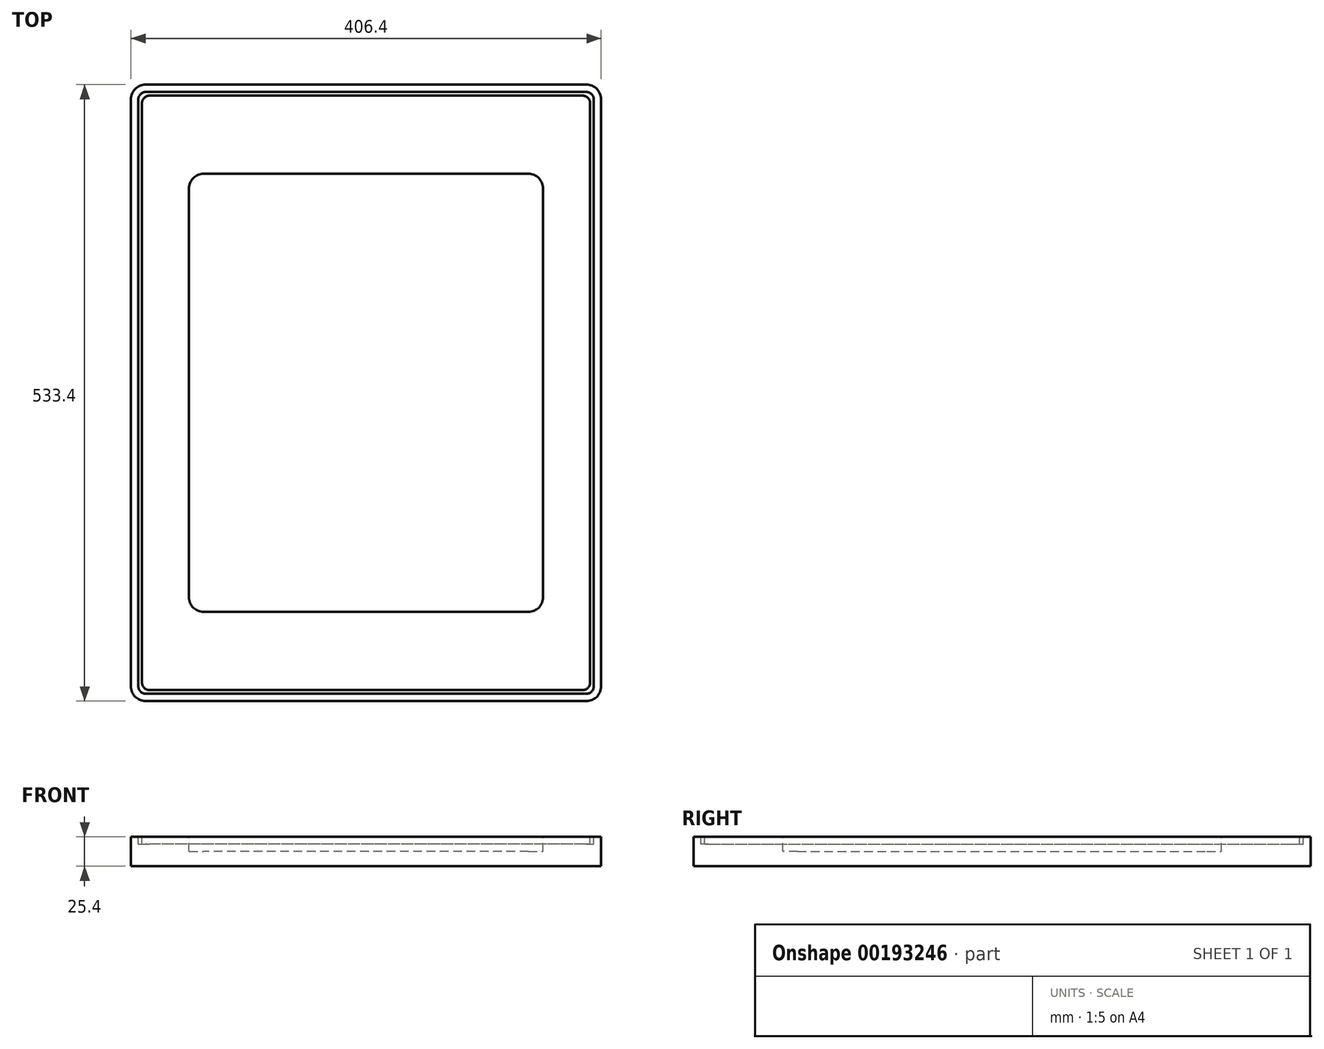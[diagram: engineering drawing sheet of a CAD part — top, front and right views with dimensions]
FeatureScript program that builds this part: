
annotation { "Feature Type Name" : "Feature", "Feature Type Description" : "" }
export const myFeature = defineFeature(function(context is Context, id is Id, definition is map)
    precondition{}
    {
        {
            var Q0;
            Q0=qCreatedBy(makeId("Top.planeOp"),FACE);
            var sketch = newSketch(context, id + "F0", { "sketchPlane" : qUnion([Q0])});
            skLineSegment(sketch, "E0.bottom", {"start": v(203.2, -266.7) * mm, "end": v(-203.2, -266.7) * mm});
            skLineSegment(sketch, "E0.top", {"start": v(203.2, 266.7) * mm, "end": v(-203.2, 266.7) * mm});
            skLineSegment(sketch, "E0.left", {"start": v(203.2, -266.7) * mm, "end": v(203.2, 266.7) * mm});
            skLineSegment(sketch, "E0.right", {"start": v(-203.2, -266.7) * mm, "end": v(-203.2, 266.7) * mm});
            skPoint(sketch, "E0.middle", {"position": v(0, 0) * mm});
            skSolve(sketch);
        }
        {
            var Q0;
            Q0=makeQuery(id+"F0.imprint","IMPRINT",FACE,{"disambiguationData":[TD([[makeQuery(id+"F0.imprint","IMPRINT",EDGE,{"derivedFrom":sQuery(id+"F0.wireOp",EDGE,"E0.bottom")}),-1.0]])]});
            extrude(context, id + "F1", {"entities" : qUnion([Q0]), "depth" : 25.4 * mm});
        }
        {
            var Q0;
            Q0=makeQuery(id+"F1.opExtrude","CAP_FACE",FACE,{"disambiguationData":[OSD([sQuery(id+"F0.wireOp",EDGE,"E0.bottom"),sQuery(id+"F0.wireOp",EDGE,"E0.top"),sQuery(id+"F0.wireOp",EDGE,"E0.left"),sQuery(id+"F0.wireOp",EDGE,"E0.right")])],"isStart":false});
            var sketch = newSketch(context, id + "F2", { "sketchPlane" : qUnion([Q0])});
            skLineSegment(sketch, "E1.bottom", {"start": v(153.03, -189.55) * mm, "end": v(-153.04, -189.55) * mm});
            skLineSegment(sketch, "E1.top", {"start": v(153.03, 189.55) * mm, "end": v(-153.04, 189.55) * mm});
            skLineSegment(sketch, "E1.left", {"start": v(153.03, -189.55) * mm, "end": v(153.03, 189.55) * mm});
            skLineSegment(sketch, "E1.right", {"start": v(-153.04, -189.55) * mm, "end": v(-153.04, 189.55) * mm});
            skPoint(sketch, "E1.middle", {"position": v(0, 0) * mm});
            skSolve(sketch);
        }
        {
            var Q0;
            Q0 = qSketchRegion(id + "F2", true);
            extrude(context, id + "F3", {"entities" : qUnion([Q0]), "operationType" : NewBodyOperationType.REMOVE, "oppositeDirection" : true, "depth" : 12.7 * mm});
        }
        {
            var Q0;
            Q0=makeQuery(id+"F1.opExtrude","SWEPT_EDGE",EDGE,{"disambiguationData":[OSD([sQuery(id+"F0.wireOp",EDGE,"E0.bottom"),sQuery(id+"F0.wireOp",EDGE,"E0.right")])]});
            var Q1;
            Q1=makeQuery(id+"F1.opExtrude","SWEPT_EDGE",EDGE,{"disambiguationData":[OSD([sQuery(id+"F0.wireOp",EDGE,"E0.bottom"),sQuery(id+"F0.wireOp",EDGE,"E0.left")])]});
            var Q2;
            Q2=makeQuery(id+"F1.opExtrude","SWEPT_EDGE",EDGE,{"disambiguationData":[OSD([sQuery(id+"F0.wireOp",EDGE,"E0.top"),sQuery(id+"F0.wireOp",EDGE,"E0.left")])]});
            var Q3;
            Q3=makeQuery(id+"F1.opExtrude","SWEPT_EDGE",EDGE,{"disambiguationData":[OSD([sQuery(id+"F0.wireOp",EDGE,"E0.top"),sQuery(id+"F0.wireOp",EDGE,"E0.right")])]});
            var Q4;
            Q4=makeQuery(id+"F3.boolean.opBoolean","COPY",EDGE,{"derivedFrom":makeQuery(id+"F3.opExtrude","SWEPT_EDGE",EDGE,{"disambiguationData":[OSD([sQuery(id+"F2.wireOp",EDGE,"E1.top"),sQuery(id+"F2.wireOp",EDGE,"E1.right")])]})});
            var Q5;
            Q5=makeQuery(id+"F3.boolean.opBoolean","COPY",EDGE,{"derivedFrom":makeQuery(id+"F3.opExtrude","SWEPT_EDGE",EDGE,{"disambiguationData":[OSD([sQuery(id+"F2.wireOp",EDGE,"E1.top"),sQuery(id+"F2.wireOp",EDGE,"E1.left")])]})});
            var Q6;
            Q6=makeQuery(id+"F3.boolean.opBoolean","COPY",EDGE,{"derivedFrom":makeQuery(id+"F3.opExtrude","SWEPT_EDGE",EDGE,{"disambiguationData":[OSD([sQuery(id+"F2.wireOp",EDGE,"E1.bottom"),sQuery(id+"F2.wireOp",EDGE,"E1.left")])]})});
            var Q7;
            Q7=makeQuery(id+"F3.boolean.opBoolean","COPY",EDGE,{"derivedFrom":makeQuery(id+"F3.opExtrude","SWEPT_EDGE",EDGE,{"disambiguationData":[OSD([sQuery(id+"F2.wireOp",EDGE,"E1.bottom"),sQuery(id+"F2.wireOp",EDGE,"E1.right")])]})});
            fillet(context, id + "F4", {"entities" : qUnion([Q0, Q1, Q2, Q3, Q4, Q5, Q6, Q7]), "radius" : 12.7 * mm, "tangentPropagation" : true, "allowEdgeOverflow" : false});
        }
        {
            var Q0;
            Q0=makeQuery(id+"F1.opExtrude","CAP_FACE",FACE,{"disambiguationData":[OSD([sQuery(id+"F0.wireOp",EDGE,"E0.bottom"),sQuery(id+"F0.wireOp",EDGE,"E0.top"),sQuery(id+"F0.wireOp",EDGE,"E0.left"),sQuery(id+"F0.wireOp",EDGE,"E0.right")])],"isStart":false});
            var sketch = newSketch(context, id + "F5", { "sketchPlane" : qUnion([Q0])});
            skArc(sketch, "E2.0", {"start": v(-196.85, -254) * mm, "mid": v(-195, -258.5) * mm, "end": v(-190.5, -260.35) * mm});
            skLineSegment(sketch, "E2.1", {"start": v(190.5, -260.35) * mm, "end": v(-190.5, -260.35) * mm});
            skLineSegment(sketch, "E2.2", {"start": v(-196.85, -254) * mm, "end": v(-196.85, 254) * mm});
            skArc(sketch, "E2.3", {"start": v(190.5, -260.35) * mm, "mid": v(195, -258.5) * mm, "end": v(196.85, -254) * mm});
            skArc(sketch, "E2.4", {"start": v(-190.5, 260.35) * mm, "mid": v(-195, 258.5) * mm, "end": v(-196.85, 254) * mm});
            skLineSegment(sketch, "E2.5", {"start": v(190.5, 260.35) * mm, "end": v(-190.5, 260.35) * mm});
            skArc(sketch, "E2.6", {"start": v(196.85, 254) * mm, "mid": v(195, 258.5) * mm, "end": v(190.5, 260.35) * mm});
            skLineSegment(sketch, "E2.7", {"start": v(196.85, -254) * mm, "end": v(196.85, 254) * mm});
            skLineSegment(sketch, "E3.0", {"start": v(-193.68, -250.83) * mm, "end": v(-193.68, 250.83) * mm});
            skLineSegment(sketch, "E3.1", {"start": v(187.32, -257.18) * mm, "end": v(-187.33, -257.18) * mm});
            skLineSegment(sketch, "E3.2", {"start": v(193.67, -250.83) * mm, "end": v(193.67, 250.83) * mm});
            skLineSegment(sketch, "E3.3", {"start": v(187.32, 257.18) * mm, "end": v(-187.33, 257.18) * mm});
            skPoint(sketch, "E4.visualSharp", {"position": v(-193.68, 257.18) * mm});
            skArc(sketch, "E4.filletArc", {"start": v(-187.33, 257.18) * mm, "mid": v(-191.82, 255.32) * mm, "end": v(-193.68, 250.83) * mm});
            skPoint(sketch, "E5.visualSharp", {"position": v(193.67, 257.18) * mm});
            skArc(sketch, "E5.filletArc", {"start": v(193.68, 250.83) * mm, "mid": v(191.82, 255.32) * mm, "end": v(187.32, 257.18) * mm});
            skPoint(sketch, "E6.visualSharp", {"position": v(193.67, -257.18) * mm});
            skArc(sketch, "E6.filletArc", {"start": v(187.32, -257.18) * mm, "mid": v(191.82, -255.32) * mm, "end": v(193.67, -250.83) * mm});
            skPoint(sketch, "E7.visualSharp", {"position": v(-193.68, -257.18) * mm});
            skArc(sketch, "E7.filletArc", {"start": v(-193.68, -250.83) * mm, "mid": v(-191.82, -255.32) * mm, "end": v(-187.33, -257.18) * mm});
            skSolve(sketch);
        }
        {
            var Q0;
            Q0 = qSketchRegion(id + "F5", true);
            extrude(context, id + "F6", {"entities" : qUnion([Q0]), "operationType" : NewBodyOperationType.REMOVE, "oppositeDirection" : true, "depth" : 6.35 * mm});
        }
    });
